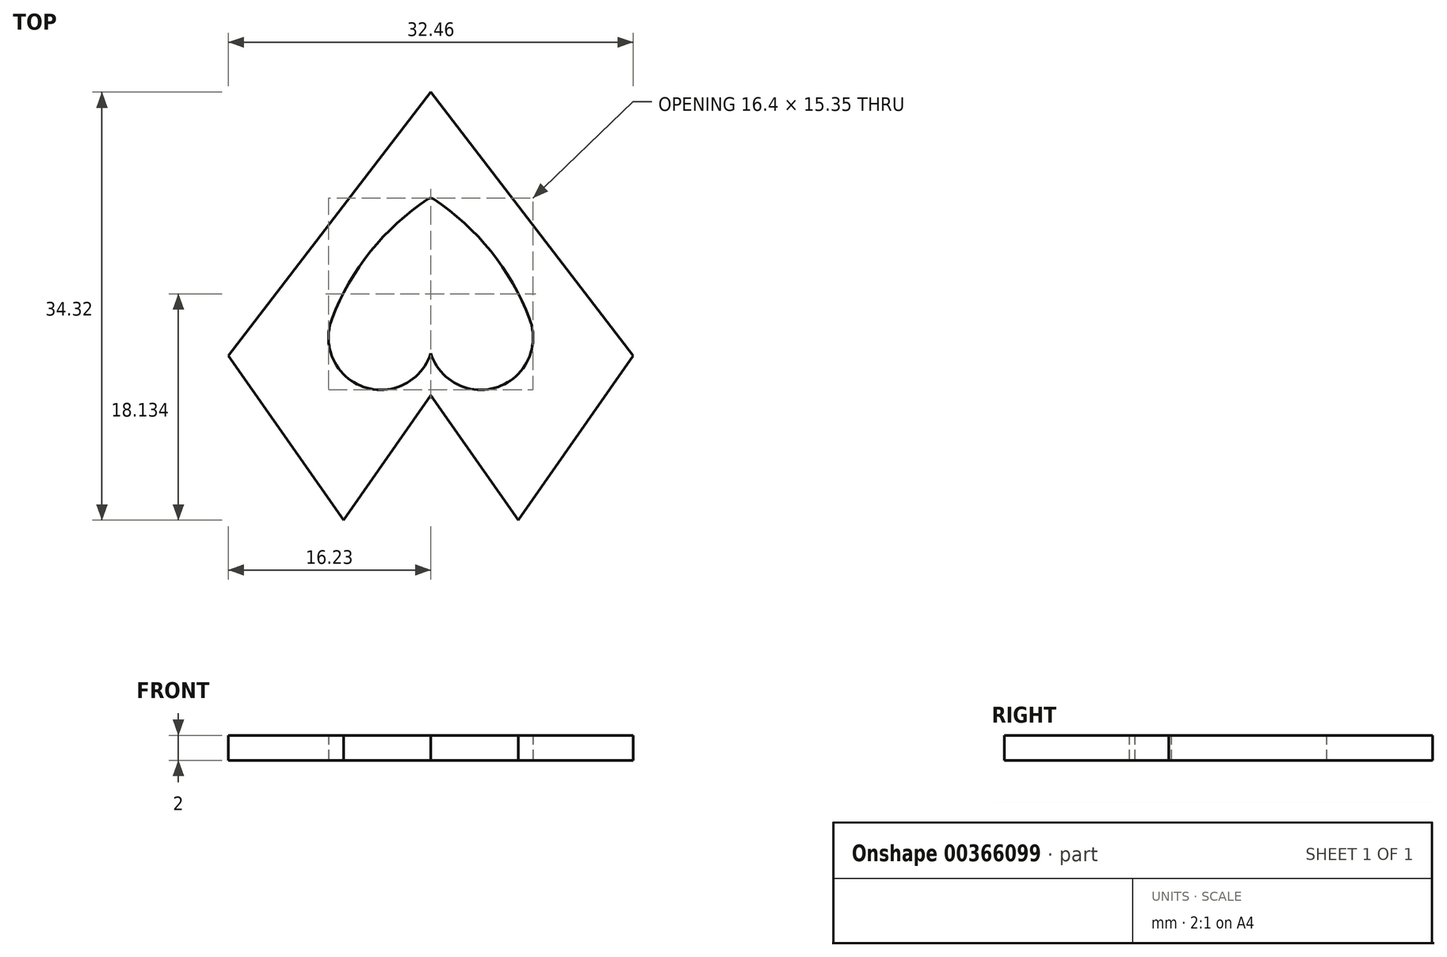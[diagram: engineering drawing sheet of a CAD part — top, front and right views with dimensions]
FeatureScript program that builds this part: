
annotation { "Feature Type Name" : "Feature", "Feature Type Description" : "" }
export const myFeature = defineFeature(function(context is Context, id is Id, definition is map)
    precondition{}
    {
        {
            var Q0;
            Q0=qCreatedBy(makeId("Top.planeOp"),FACE);
            var sketch = newSketch(context, id + "F0", { "sketchPlane" : qUnion([Q0])});
            skLineSegment(sketch, "E0", {"start": v(0, -10) * mm, "end": v(7, -20) * mm});
            skLineSegment(sketch, "E1", {"start": v(7, -20) * mm, "end": v(16.48, -6.47) * mm});
            skLineSegment(sketch, "E2", {"start": v(16.48, -6.47) * mm, "end": v(0, 15) * mm});
            skLineSegment(sketch, "E3", {"start": v(0, 0) * mm, "end": v(0, -10) * mm, "construction": true});
            skLineSegment(sketch, "E4", {"start": v(0, 0) * mm, "end": v(0, 15) * mm, "construction": true});
            skLineSegment(sketch, "E5.MirrorCS", {"start": v(0, -10) * mm, "end": v(-7, -20) * mm});
            skLineSegment(sketch, "E6.MirrorCS", {"start": v(-7, -20) * mm, "end": v(-16.48, -6.47) * mm});
            skLineSegment(sketch, "E7.MirrorCS", {"start": v(-16.48, -6.47) * mm, "end": v(0, 15) * mm});
            skArc(sketch, "E8", {"start": v(-0.11, 5.93) * mm, "mid": v(-4.66, 1.78) * mm, "end": v(-7.73, -3.56) * mm});
            skArc(sketch, "E9", {"start": v(-7.73, -3.56) * mm, "mid": v(-5.33, -8.77) * mm, "end": v(-0.2, -6.22) * mm});
            skArc(sketch, "E10.MirrorCS", {"start": v(7.73, -3.56) * mm, "mid": v(5.33, -8.77) * mm, "end": v(0.2, -6.22) * mm});
            skArc(sketch, "E11.MirrorCS", {"start": v(0.11, 5.93) * mm, "mid": v(4.66, 1.78) * mm, "end": v(7.73, -3.56) * mm});
            skLineSegment(sketch, "E12.0", {"start": v(0, -9.65) * mm, "end": v(7, -19.65) * mm});
            skLineSegment(sketch, "E12.1", {"start": v(16.23, -6.48) * mm, "end": v(0, 14.67) * mm});
            skLineSegment(sketch, "E12.2", {"start": v(-16.23, -6.48) * mm, "end": v(0, 14.67) * mm});
            skLineSegment(sketch, "E12.3", {"start": v(7, -19.65) * mm, "end": v(16.23, -6.48) * mm});
            skLineSegment(sketch, "E12.4", {"start": v(-7, -19.65) * mm, "end": v(-16.23, -6.48) * mm});
            skLineSegment(sketch, "E12.5", {"start": v(0, -9.65) * mm, "end": v(-7, -19.65) * mm});
            skPoint(sketch, "E13.visualSharp", {"position": v(0, -5) * mm});
            skArc(sketch, "E13.filletArc", {"start": v(0.2, -6.22) * mm, "mid": v(0, -6.08) * mm, "end": v(-0.2, -6.22) * mm});
            skPoint(sketch, "E14.visualSharp", {"position": v(0, 6) * mm});
            skArc(sketch, "E14.filletArc", {"start": v(0.11, 5.93) * mm, "mid": v(0, 5.96) * mm, "end": v(-0.11, 5.93) * mm});
            skArc(sketch, "E15.0", {"start": v(-7.92, -3.5) * mm, "mid": v(-5.4, -8.96) * mm, "end": v(0, -6.28) * mm});
            skArc(sketch, "E15.1", {"start": v(7.92, -3.5) * mm, "mid": v(5.4, -8.96) * mm, "end": v(0, -6.28) * mm});
            skArc(sketch, "E15.2", {"start": v(-0.22, 6.1) * mm, "mid": v(-4.82, 1.9) * mm, "end": v(-7.92, -3.5) * mm});
            skArc(sketch, "E15.3", {"start": v(0.22, 6.1) * mm, "mid": v(0, 6.16) * mm, "end": v(-0.22, 6.1) * mm});
            skArc(sketch, "E15.4", {"start": v(0.22, 6.1) * mm, "mid": v(4.82, 1.9) * mm, "end": v(7.92, -3.5) * mm});
            skSolve(sketch);
        }
        {
            var Q0;
            Q0=makeQuery(id+"F0.imprint","IMPRINT",FACE,{"disambiguationData":[TD([[makeQuery(id+"F0.imprint","IMPRINT",EDGE,{"derivedFrom":sQuery(id+"F0.wireOp",EDGE,"E12.0")}),1.0]])]});
            extrude(context, id + "F1", {"entities" : qUnion([Q0]), "depth" : 2 * mm});
        }
    });
